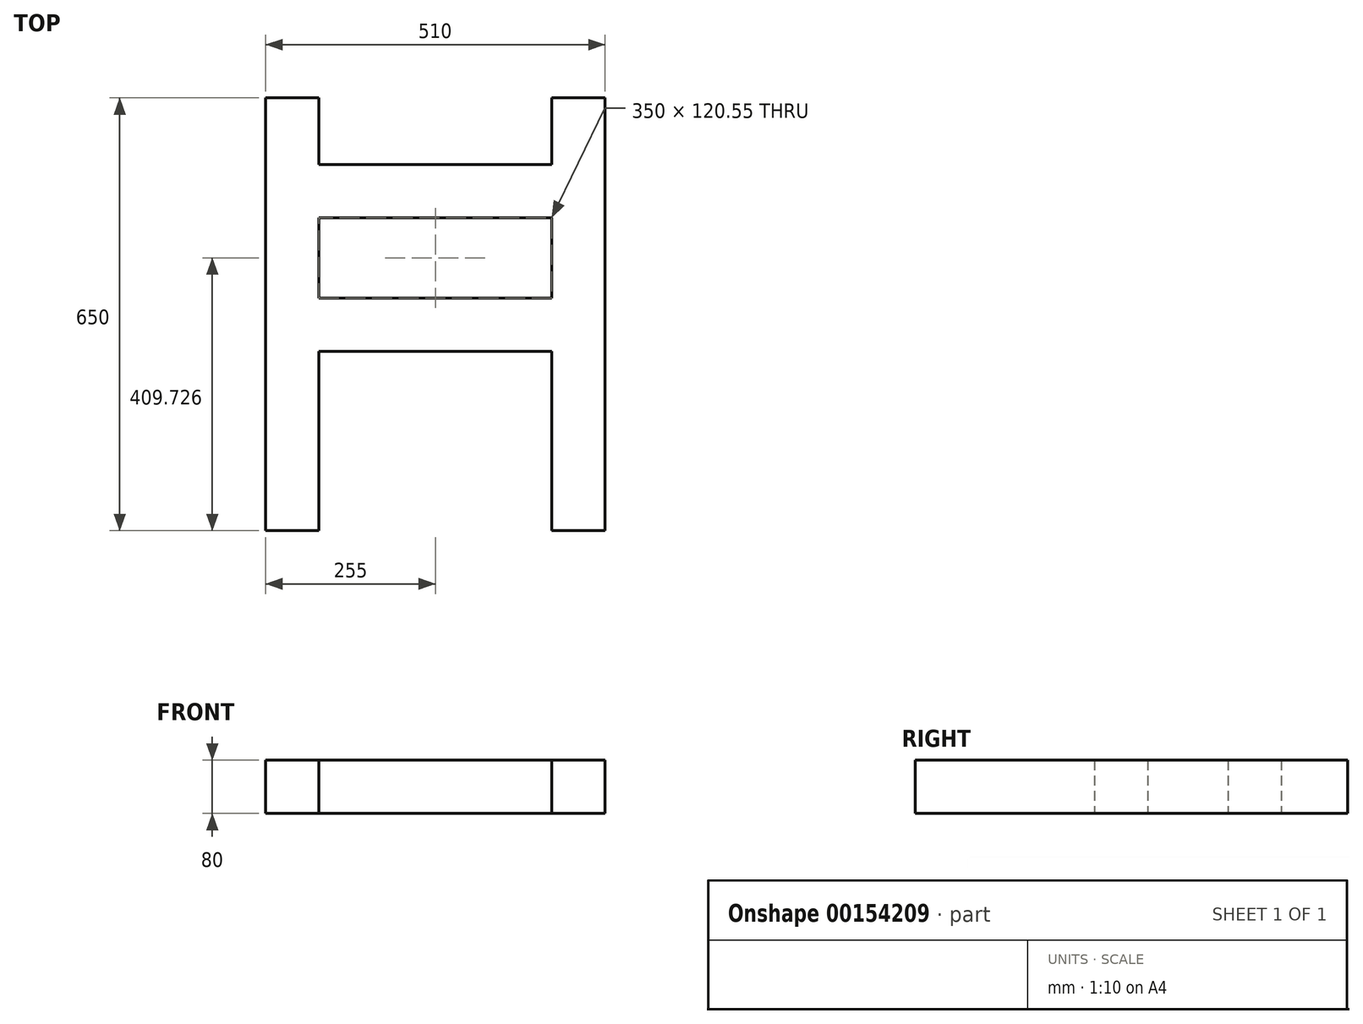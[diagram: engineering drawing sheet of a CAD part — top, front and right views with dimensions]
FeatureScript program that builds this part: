
annotation { "Feature Type Name" : "Feature", "Feature Type Description" : "" }
export const myFeature = defineFeature(function(context is Context, id is Id, definition is map)
    precondition{}
    {
        {
            var Q0;
            Q0=qCreatedBy(makeId("Top.planeOp"),FACE);
            var sketch = newSketch(context, id + "F0", { "sketchPlane" : qUnion([Q0])});
            skLineSegment(sketch, "E0.bottom", {"start": v(0, 0) * mm, "end": v(80, 0) * mm});
            skLineSegment(sketch, "E0.top", {"start": v(0, 650) * mm, "end": v(80, 650) * mm});
            skLineSegment(sketch, "E0.left", {"start": v(0, 0) * mm, "end": v(0, 650) * mm});
            skLineSegment(sketch, "E0.right", {"start": v(80, 0) * mm, "end": v(80, 650) * mm});
            skLineSegment(sketch, "E1.bottom", {"start": v(80, 550) * mm, "end": v(430, 550) * mm});
            skLineSegment(sketch, "E1.top", {"start": v(80, 470) * mm, "end": v(430, 470) * mm});
            skLineSegment(sketch, "E1.left", {"start": v(80, 550) * mm, "end": v(80, 470) * mm});
            skLineSegment(sketch, "E1.right", {"start": v(430, 550) * mm, "end": v(430, 470) * mm});
            skLineSegment(sketch, "E2.bottom", {"start": v(80, 349.45) * mm, "end": v(430, 349.45) * mm});
            skLineSegment(sketch, "E2.top", {"start": v(79.95, 269.45) * mm, "end": v(430, 269.45) * mm});
            skLineSegment(sketch, "E2.right", {"start": v(430, 349.45) * mm, "end": v(430, 269.45) * mm});
            skLineSegment(sketch, "E3", {"start": v(80, 349.45) * mm, "end": v(79.95, 269.45) * mm});
            skPoint(sketch, "E4.firstSnap0", {"position": v(40, 650) * mm});
            skLineSegment(sketch, "E4.bottom", {"start": v(430, 650) * mm, "end": v(510, 650) * mm});
            skLineSegment(sketch, "E4.top", {"start": v(430, 0) * mm, "end": v(510, 0) * mm});
            skLineSegment(sketch, "E4.left", {"start": v(430, 650) * mm, "end": v(430, 0) * mm});
            skLineSegment(sketch, "E4.right", {"start": v(510, 650) * mm, "end": v(510, 0) * mm});
            skSolve(sketch);
        }
        {
            var Q0;
            Q0 = qSketchRegion(id + "F0", true);
            extrude(context, id + "F1", {"entities" : qUnion([Q0]), "depth" : 80 * mm});
        }
    });
